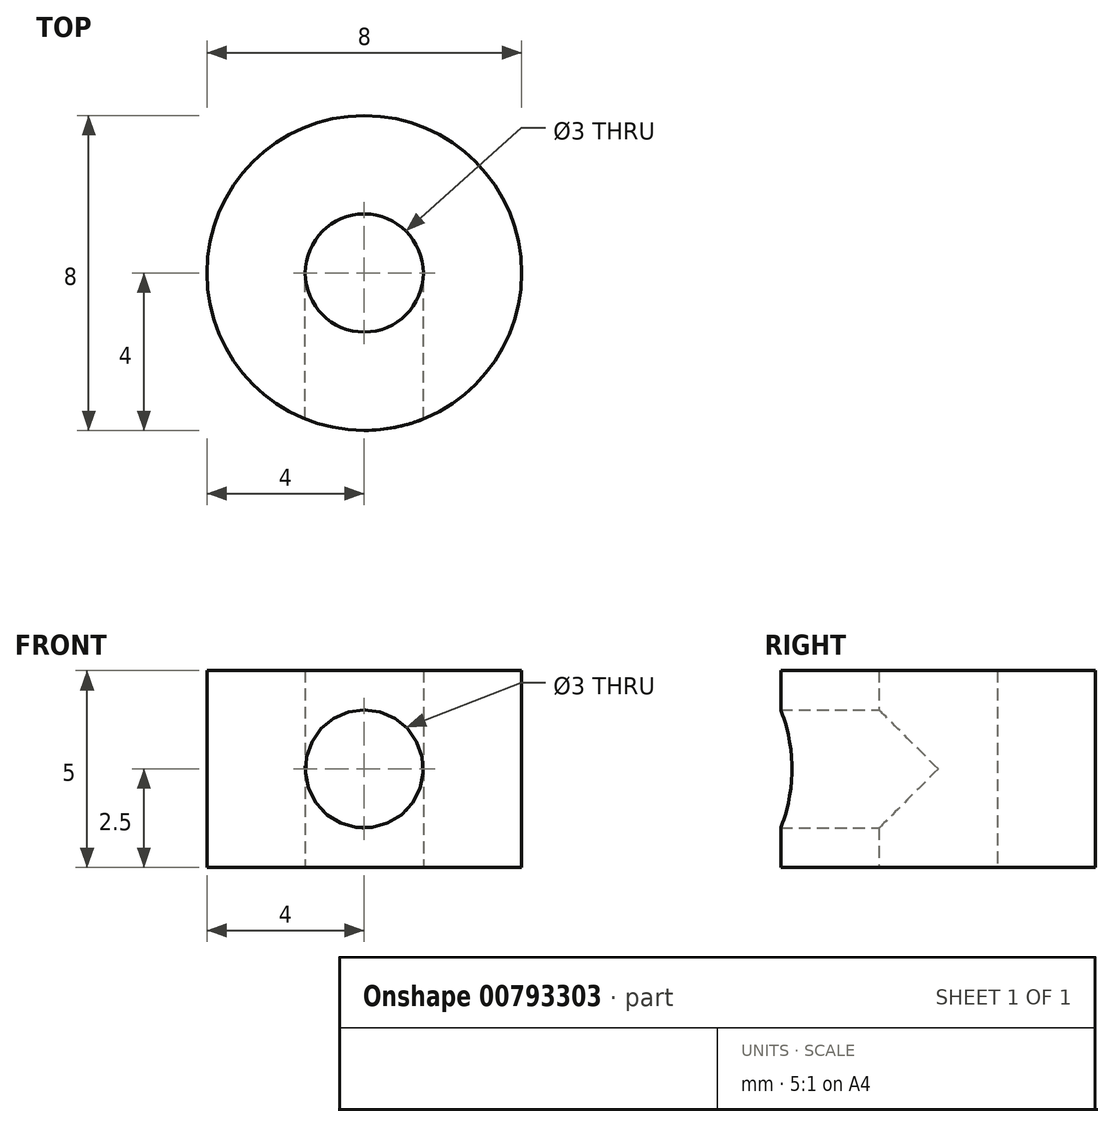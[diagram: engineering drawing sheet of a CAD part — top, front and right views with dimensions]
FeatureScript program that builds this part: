
annotation { "Feature Type Name" : "Feature", "Feature Type Description" : "" }
export const myFeature = defineFeature(function(context is Context, id is Id, definition is map)
    precondition{}
    {
        {
            var Q0;
            Q0=qCreatedBy(makeId("Top.planeOp"),FACE);
            var sketch = newSketch(context, id + "F0", { "sketchPlane" : qUnion([Q0])});
            skCircle(sketch, "E0", {"center": v(0, 0) * mm, "radius": 4 * mm});
            skCircle(sketch, "E1", {"center": v(0, 0) * mm, "radius": 1.5 * mm});
            skSolve(sketch);
        }
        {
            var Q0;
            Q0=qSketchRegion(id+"F0",true);
            extrude(context, id + "F1", {"entities" : qUnion([Q0]), "depth" : 5 * mm, "offsetDistance" : 25 * mm});
        }
        {
            var Q0;
            Q0=qCreatedBy(makeId("Front.planeOp"),FACE);
            var sketch = newSketch(context, id + "F2", { "sketchPlane" : qUnion([Q0])});
            skCircle(sketch, "E2", {"center": v(0, 2.5) * mm, "radius": 1.5 * mm});
            skSolve(sketch);
        }
        {
            var Q0;
            Q0=qSketchRegion(id+"F2",true);
            extrude(context, id + "F3", {"entities" : qUnion([Q0]), "operationType" : NewBodyOperationType.REMOVE, "depth" : 25 * mm, "offsetDistance" : 25 * mm});
        }
    });
